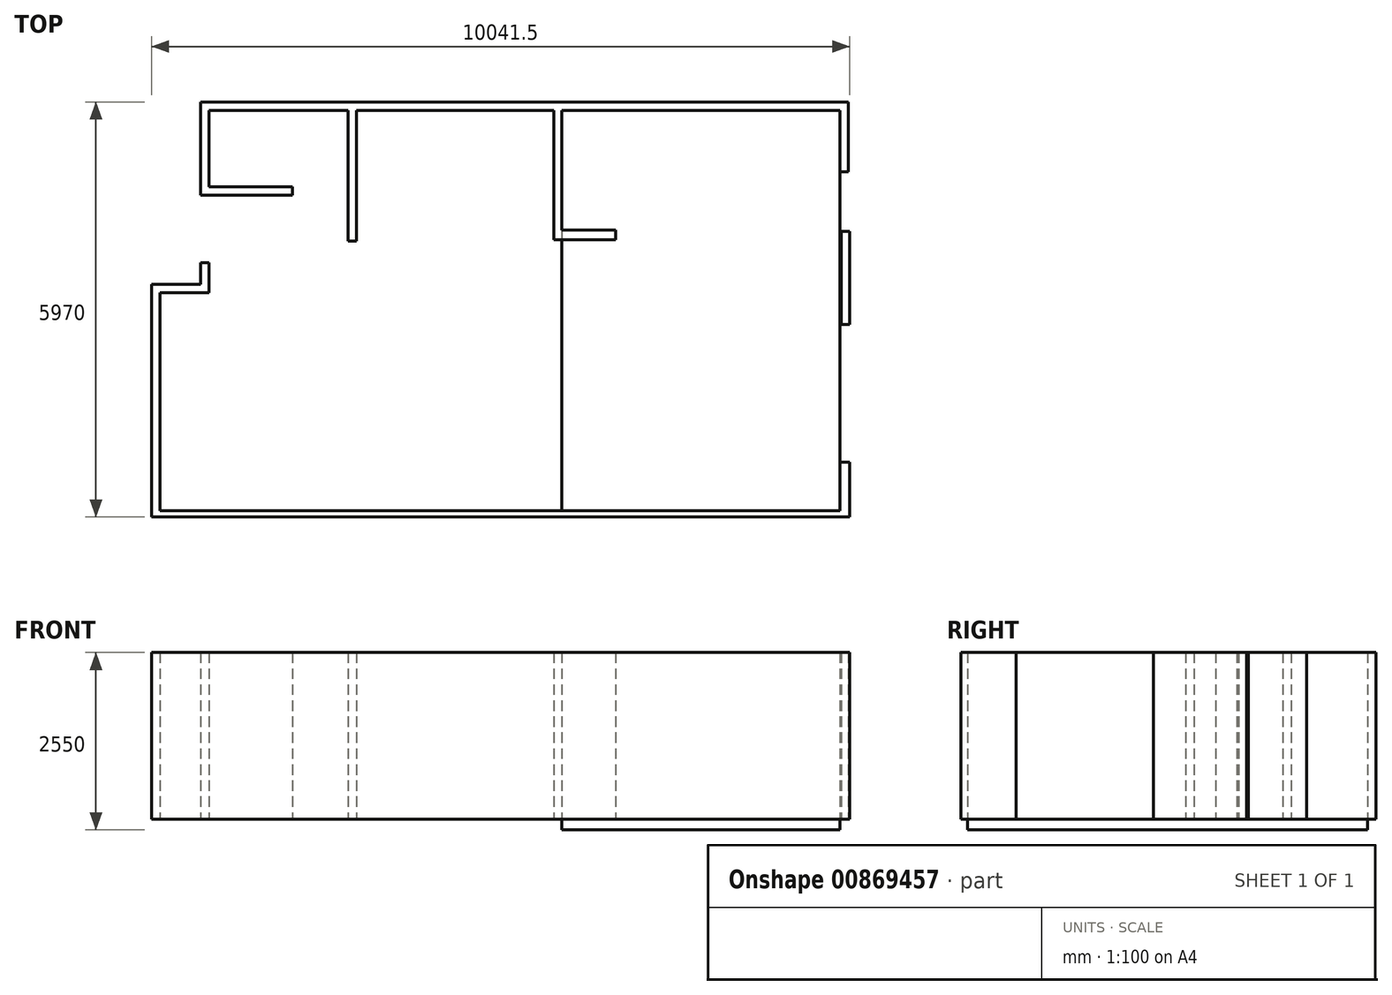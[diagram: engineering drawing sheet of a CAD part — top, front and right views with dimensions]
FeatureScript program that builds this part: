
annotation { "Feature Type Name" : "Feature", "Feature Type Description" : "" }
export const myFeature = defineFeature(function(context is Context, id is Id, definition is map)
    precondition{}
    {
        {
            var Q0;
            Q0=qCreatedBy(makeId("Top.planeOp"),FACE);
            var sketch = newSketch(context, id + "F0", { "sketchPlane" : qUnion([Q0])});
            skLineSegment(sketch, "E0", {"start": v(0, 0) * mm, "end": v(21000, 0) * mm, "construction": true});
            skLineSegment(sketch, "E1", {"start": v(11408.87, -112.07) * mm, "end": v(11408.87, -1892.8) * mm});
            skLineSegment(sketch, "E2", {"start": v(11408.87, -1892.8) * mm, "end": v(12155.09, -1892.8) * mm});
            skLineSegment(sketch, "E3", {"start": v(12155.09, -1892.8) * mm, "end": v(12155.09, -2020) * mm});
            skLineSegment(sketch, "E4", {"start": v(12155.09, -2020) * mm, "end": v(11264.72, -2020) * mm});
            skLineSegment(sketch, "E5", {"start": v(11264.72, -2020) * mm, "end": v(11264.72, -112.07) * mm});
            skLineSegment(sketch, "E6", {"start": v(11264.72, -112.07) * mm, "end": v(8430.92, -112.07) * mm});
            skLineSegment(sketch, "E7", {"start": v(8430.92, -112.07) * mm, "end": v(8430.92, -1993.76) * mm});
            skLineSegment(sketch, "E8", {"start": v(8430.92, -1993.76) * mm, "end": v(8288.3, -1993.76) * mm});
            skLineSegment(sketch, "E9", {"start": v(8288.3, -1993.76) * mm, "end": v(8288.3, -112.07) * mm});
            skLineSegment(sketch, "E10", {"start": v(8288.3, -112.07) * mm, "end": v(6302.23, -112.07) * mm});
            skLineSegment(sketch, "E11", {"start": v(6302.23, -112.07) * mm, "end": v(6302.23, -1232.23) * mm});
            skLineSegment(sketch, "E12", {"start": v(6302.23, -1232.23) * mm, "end": v(7507.29, -1232.23) * mm});
            skLineSegment(sketch, "E13", {"start": v(7507.29, -1232.23) * mm, "end": v(7507.29, -1353.24) * mm});
            skLineSegment(sketch, "E14", {"start": v(7507.29, -1353.24) * mm, "end": v(6181.22, -1353.24) * mm});
            skLineSegment(sketch, "E15", {"start": v(15518.59, -992.12) * mm, "end": v(15386.67, -992.12) * mm});
            skLineSegment(sketch, "E16", {"start": v(15386.67, -992.12) * mm, "end": v(15386.67, -112.07) * mm});
            skLineSegment(sketch, "E17", {"start": v(15518.59, -992.12) * mm, "end": v(15518.59, 0) * mm});
            skLineSegment(sketch, "E18.bottom", {"start": v(15512.16, -3210.92) * mm, "end": v(15380.25, -3210.92) * mm});
            skLineSegment(sketch, "E18.top", {"start": v(15512.16, -1866.8) * mm, "end": v(15380.25, -1866.8) * mm});
            skLineSegment(sketch, "E18.left", {"start": v(15512.16, -3210.92) * mm, "end": v(15512.16, -1866.8) * mm});
            skLineSegment(sketch, "E18.right", {"start": v(15380.25, -3210.92) * mm, "end": v(15380.25, -1866.8) * mm});
            skLineSegment(sketch, "E19", {"start": v(15499.43, -5194.69) * mm, "end": v(15499.43, -5998.9) * mm});
            skLineSegment(sketch, "E20", {"start": v(15499.43, -5998.9) * mm, "end": v(5468.29, -5998.9) * mm});
            skLineSegment(sketch, "E21", {"start": v(5468.29, -5998.9) * mm, "end": v(5468.29, -2605.2) * mm});
            skLineSegment(sketch, "E22", {"start": v(5468.29, -2605.2) * mm, "end": v(6177.08, -2605.2) * mm});
            skLineSegment(sketch, "E23", {"start": v(6177.08, -2605.2) * mm, "end": v(6177.08, -2304.99) * mm});
            skLineSegment(sketch, "E24", {"start": v(6177.08, -2304.99) * mm, "end": v(6302.37, -2304.99) * mm});
            skLineSegment(sketch, "E25", {"start": v(6302.37, -2304.99) * mm, "end": v(6302.37, -2729.25) * mm});
            skLineSegment(sketch, "E26", {"start": v(6302.37, -2729.25) * mm, "end": v(5610.7, -2729.25) * mm});
            skLineSegment(sketch, "E27", {"start": v(5610.7, -2729.25) * mm, "end": v(5610.7, -5844.52) * mm});
            skLineSegment(sketch, "E28", {"start": v(5610.7, -5844.52) * mm, "end": v(15371.72, -5844.52) * mm});
            skLineSegment(sketch, "E29", {"start": v(15371.72, -5844.52) * mm, "end": v(15371.72, -5194.69) * mm});
            skLineSegment(sketch, "E30", {"start": v(15371.72, -5194.69) * mm, "end": v(15499.43, -5194.69) * mm});
            skLineSegment(sketch, "E31", {"start": v(6181.22, -1353.24) * mm, "end": v(6177.08, 0) * mm});
            skPoint(sketch, "E32", {"position": v(0, 0) * mm});
            skLineSegment(sketch, "E33", {"start": v(11408.87, -112.07) * mm, "end": v(15386.67, -112.07) * mm});
            skLineSegment(sketch, "E34", {"start": v(6177.08, 0) * mm, "end": v(15518.59, 0) * mm});
            skSolve(sketch);
        }
        {
            var Q0;
            Q0=qCreatedBy(makeId("Top.planeOp"),FACE);
            var sketch = newSketch(context, id + "F1", { "sketchPlane" : qUnion([Q0])});
            skLineSegment(sketch, "E35", {"start": v(0, 0) * mm, "end": v(21000, 0) * mm, "construction": true});
            skLineSegment(sketch, "E36", {"start": v(11380, -120) * mm, "end": v(11380, -1840) * mm});
            skLineSegment(sketch, "E37", {"start": v(11380, -1840) * mm, "end": v(12150, -1840) * mm});
            skLineSegment(sketch, "E38", {"start": v(12150, -1840) * mm, "end": v(12150, -1980) * mm});
            skLineSegment(sketch, "E39", {"start": v(12150, -1980) * mm, "end": v(11260, -1980) * mm});
            skLineSegment(sketch, "E40", {"start": v(11260, -1980) * mm, "end": v(11260, -120) * mm});
            skLineSegment(sketch, "E41", {"start": v(11260, -120) * mm, "end": v(8424.72, -120) * mm});
            skLineSegment(sketch, "E42", {"start": v(8424.72, -120) * mm, "end": v(8424.72, -2000) * mm});
            skLineSegment(sketch, "E43", {"start": v(8424.72, -2000) * mm, "end": v(8304.72, -2000) * mm});
            skLineSegment(sketch, "E44", {"start": v(8304.72, -2000) * mm, "end": v(8304.72, -120) * mm});
            skLineSegment(sketch, "E45", {"start": v(8304.72, -120) * mm, "end": v(6304.72, -120) * mm});
            skLineSegment(sketch, "E46", {"start": v(6304.72, -120) * mm, "end": v(6304.72, -1220) * mm});
            skLineSegment(sketch, "E47", {"start": v(6304.72, -1220) * mm, "end": v(7504.72, -1220) * mm});
            skLineSegment(sketch, "E48", {"start": v(7504.72, -1220) * mm, "end": v(7504.72, -1340) * mm});
            skLineSegment(sketch, "E49", {"start": v(7504.72, -1340) * mm, "end": v(6184.72, -1340) * mm});
            skLineSegment(sketch, "E50", {"start": v(15500, -1000) * mm, "end": v(15380, -1000) * mm});
            skLineSegment(sketch, "E51", {"start": v(15380, -1000) * mm, "end": v(15380, -120) * mm});
            skLineSegment(sketch, "E52", {"start": v(15500, -1000) * mm, "end": v(15500, 0) * mm});
            skLineSegment(sketch, "E53.bottom", {"start": v(15518.59, -3200) * mm, "end": v(15398.59, -3200) * mm});
            skLineSegment(sketch, "E53.top", {"start": v(15518.59, -1860) * mm, "end": v(15398.59, -1860) * mm});
            skLineSegment(sketch, "E53.left", {"start": v(15518.59, -3200) * mm, "end": v(15518.59, -1860) * mm});
            skLineSegment(sketch, "E53.right", {"start": v(15398.59, -3200) * mm, "end": v(15398.59, -1860) * mm});
            skLineSegment(sketch, "E54", {"start": v(15518.59, -5180) * mm, "end": v(15518.59, -5970) * mm});
            skLineSegment(sketch, "E55", {"start": v(15518.59, -5970) * mm, "end": v(5477.08, -5970) * mm});
            skLineSegment(sketch, "E56", {"start": v(5477.08, -5970) * mm, "end": v(5477.08, -2620) * mm});
            skLineSegment(sketch, "E57", {"start": v(5477.08, -2620) * mm, "end": v(6184.72, -2620) * mm});
            skLineSegment(sketch, "E58", {"start": v(6184.72, -2620) * mm, "end": v(6184.72, -2310) * mm});
            skLineSegment(sketch, "E59", {"start": v(6184.72, -2310) * mm, "end": v(6304.72, -2310) * mm});
            skLineSegment(sketch, "E60", {"start": v(6304.72, -2310) * mm, "end": v(6304.72, -2740) * mm});
            skLineSegment(sketch, "E61", {"start": v(6304.72, -2740) * mm, "end": v(5597.08, -2740) * mm});
            skLineSegment(sketch, "E62", {"start": v(5597.08, -2740) * mm, "end": v(5597.08, -5878.9) * mm});
            skLineSegment(sketch, "E63", {"start": v(5597.08, -5878.9) * mm, "end": v(15380.25, -5878.9) * mm});
            skLineSegment(sketch, "E64", {"start": v(15380.25, -5878.9) * mm, "end": v(15380.25, -5180) * mm});
            skLineSegment(sketch, "E65", {"start": v(15380.25, -5180) * mm, "end": v(15518.59, -5180) * mm});
            skLineSegment(sketch, "E66", {"start": v(6184.72, -1340) * mm, "end": v(6184.72, 0) * mm});
            skPoint(sketch, "E67", {"position": v(0, 0) * mm});
            skLineSegment(sketch, "E68", {"start": v(11380, -120) * mm, "end": v(15380, -120) * mm});
            skLineSegment(sketch, "E69", {"start": v(6184.72, 0) * mm, "end": v(15500, 0) * mm});
            skLineSegment(sketch, "E70", {"start": v(11260, -120) * mm, "end": v(11380, -120) * mm, "construction": true});
            skPoint(sketch, "E71", {"position": v(11320, -120) * mm});
            skPoint(sketch, "E72", {"position": v(15440, -1000) * mm});
            skLineSegment(sketch, "E73", {"start": v(8304.72, -120) * mm, "end": v(8424.72, -120) * mm, "construction": true});
            skPoint(sketch, "E74", {"position": v(8364.72, -120) * mm});
            skSolve(sketch);
        }
        {
            var Q0;
            Q0 = qSketchRegion(id + "F1", true);
            extrude(context, id + "F2", {"entities" : qUnion([Q0]), "depth" : 2400 * mm, "offsetDistance" : 25 * mm});
        }
        {
            var Q0;
            Q0=qCreatedBy(makeId("Top.planeOp"),FACE);
            var sketch = newSketch(context, id + "F3", { "sketchPlane" : qUnion([Q0])});
            skLineSegment(sketch, "E75.0", {"start": v(11380, -120) * mm, "end": v(11380, -5878.9) * mm});
            skLineSegment(sketch, "E75.2", {"start": v(11380, -120) * mm, "end": v(15380, -120) * mm});
            skLineSegment(sketch, "E76.0", {"start": v(11380, -5878.9) * mm, "end": v(15380.25, -5878.9) * mm});
            skLineSegment(sketch, "E77", {"start": v(15380.25, -5878.9) * mm, "end": v(15380, -120) * mm});
            skSolve(sketch);
        }
        {
            var Q0;
            Q0=makeQuery(id+"F3.imprint","IMPRINT",FACE,{"disambiguationData":[TD([[makeQuery(id+"F3.imprint","IMPRINT",EDGE,{"derivedFrom":sQuery(id+"F3.wireOp",EDGE,"E75.0")}),1.0]])]});
            extrude(context, id + "F4", {"entities" : qUnion([Q0]), "oppositeDirection" : true, "depth" : 150 * mm, "offsetDistance" : 25 * mm});
        }
    });
